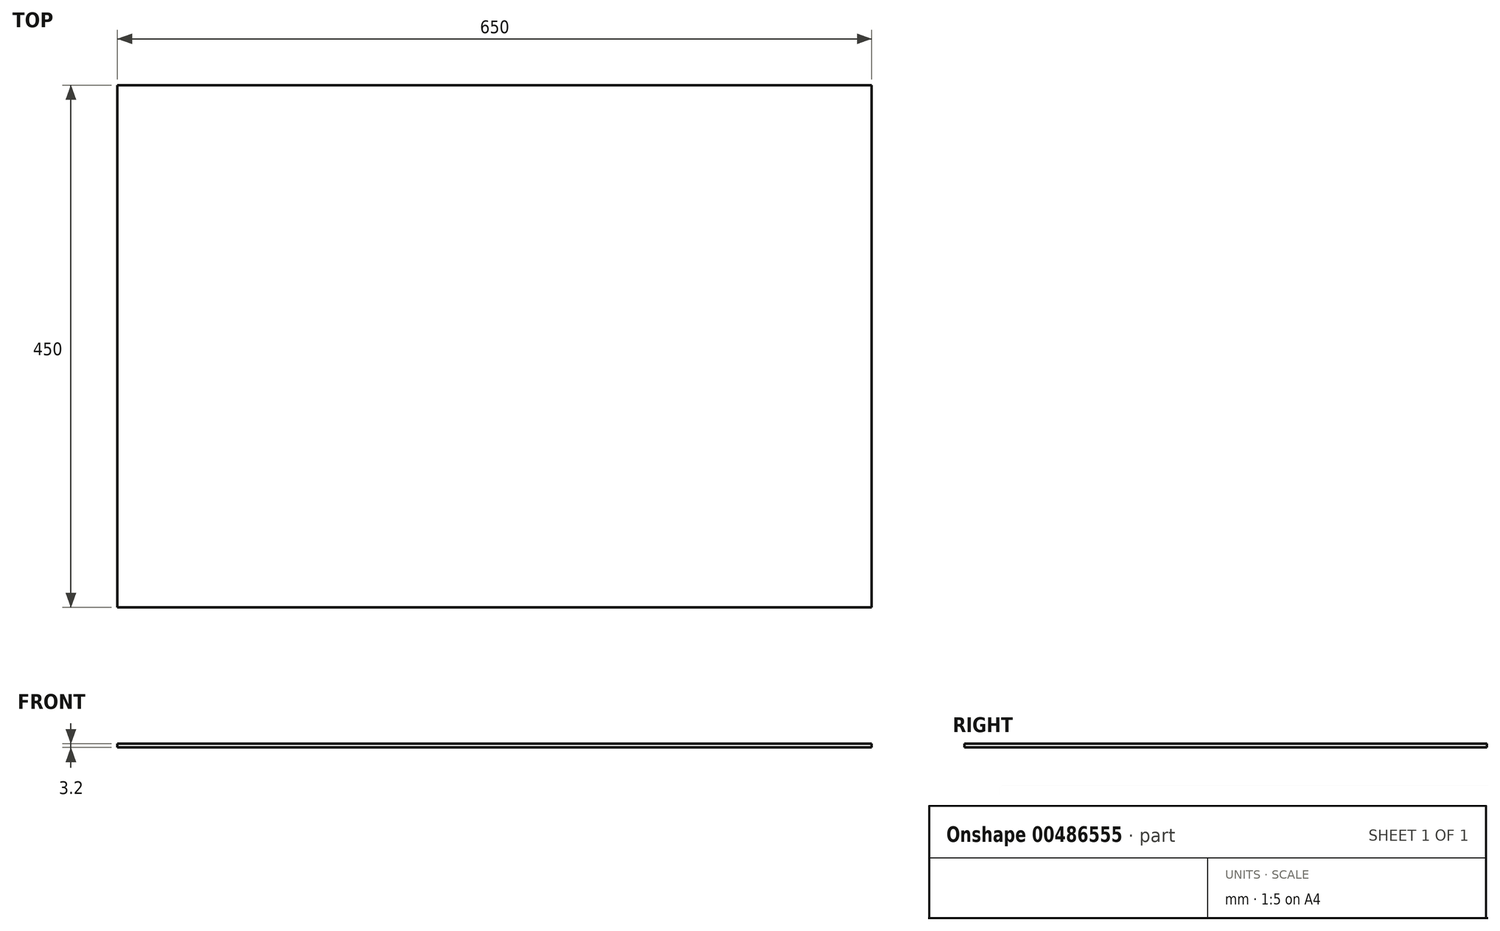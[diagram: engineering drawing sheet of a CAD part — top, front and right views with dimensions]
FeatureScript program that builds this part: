
annotation { "Feature Type Name" : "Feature", "Feature Type Description" : "" }
export const myFeature = defineFeature(function(context is Context, id is Id, definition is map)
    precondition{}
    {
        {
            var Q0;
            Q0=qCreatedBy(makeId("Top.planeOp"),FACE);
            var sketch = newSketch(context, id + "F0", { "sketchPlane" : qUnion([Q0])});
            skLineSegment(sketch, "E0.bottom", {"start": v(596.13, 424.1) * mm, "end": v(-53.87, 424.1) * mm});
            skLineSegment(sketch, "E0.top", {"start": v(596.13, -25.9) * mm, "end": v(-53.87, -25.9) * mm});
            skLineSegment(sketch, "E0.left", {"start": v(596.13, 424.1) * mm, "end": v(596.13, -25.9) * mm});
            skLineSegment(sketch, "E0.right", {"start": v(-53.87, 424.1) * mm, "end": v(-53.87, -25.9) * mm});
            skPoint(sketch, "E0.middle", {"position": v(271.13, 199.1) * mm});
            skSolve(sketch);
        }
        {
            var Q0;
            Q0 = qSketchRegion(id + "F0", true);
            extrude(context, id + "F1", {"entities" : qUnion([Q0]), "depth" : 3.2 * mm, "offsetDistance" : 25 * mm});
        }
    });
